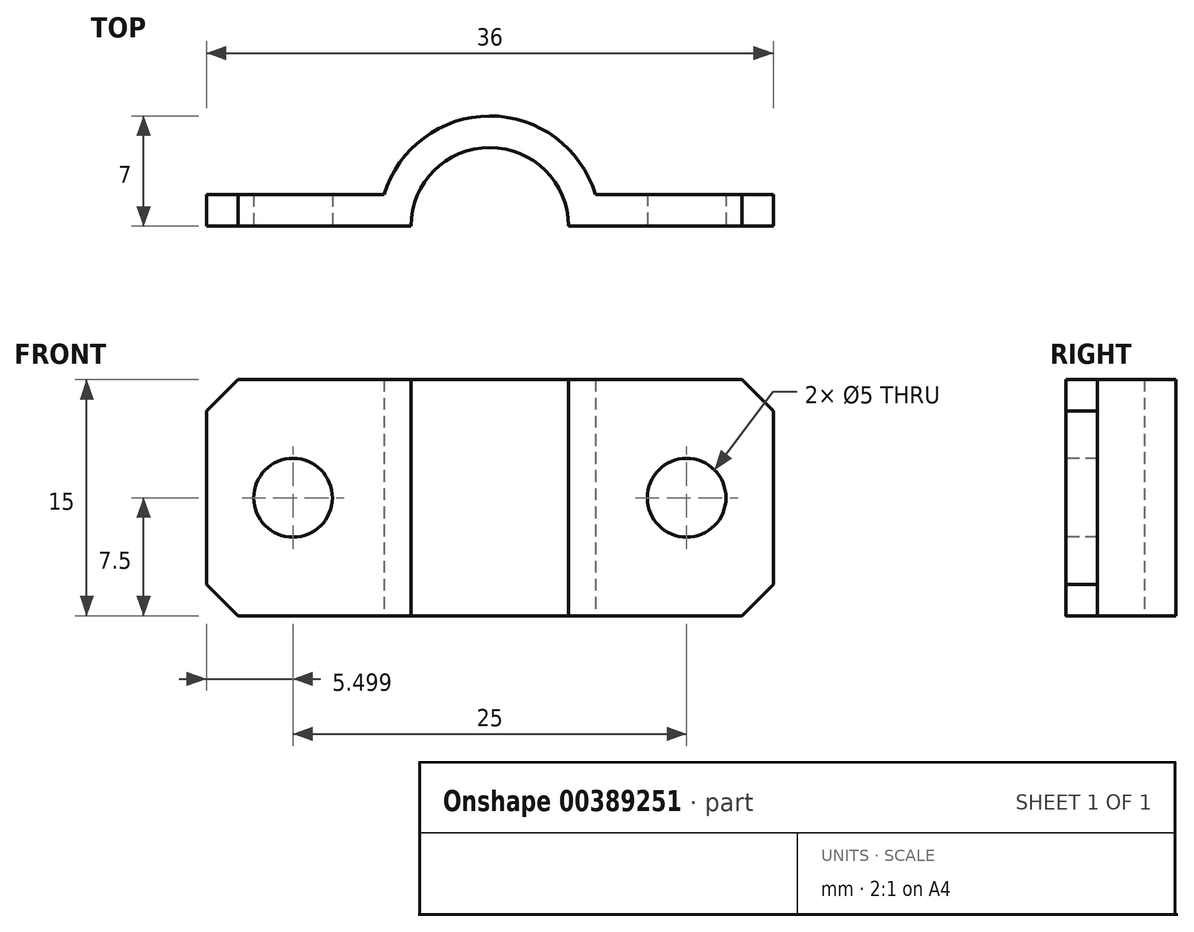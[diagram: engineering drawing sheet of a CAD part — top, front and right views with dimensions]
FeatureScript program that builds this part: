
annotation { "Feature Type Name" : "Feature", "Feature Type Description" : "" }
export const myFeature = defineFeature(function(context is Context, id is Id, definition is map)
    precondition{}
    {
        {
            var Q0;
            Q0=qCreatedBy(makeId("Top.planeOp"),FACE);
            var sketch = newSketch(context, id + "F0", { "sketchPlane" : qUnion([Q0])});
            skLineSegment(sketch, "E0", {"start": v(-47.37, 0) * mm, "end": v(-34.37, 0) * mm});
            skArc(sketch, "E1", {"start": v(-24.37, 0.02) * mm, "mid": v(-29.38, 5) * mm, "end": v(-34.37, 0) * mm});
            skLineSegment(sketch, "E2", {"start": v(-24.37, 0.02) * mm, "end": v(-34.37, 0) * mm, "construction": true});
            skLineSegment(sketch, "E3", {"start": v(-24.37, 0.02) * mm, "end": v(-11.37, 0.02) * mm});
            skLineSegment(sketch, "E4.0", {"start": v(-47.37, 2) * mm, "end": v(-36.08, 2) * mm});
            skArc(sketch, "E4.1", {"start": v(-22.67, 2.02) * mm, "mid": v(-29.38, 7) * mm, "end": v(-36.08, 2) * mm});
            skLineSegment(sketch, "E4.2", {"start": v(-22.67, 2.02) * mm, "end": v(-11.37, 2.02) * mm});
            skLineSegment(sketch, "E5", {"start": v(-11.37, 2.02) * mm, "end": v(-11.37, 0.02) * mm});
            skLineSegment(sketch, "E6", {"start": v(-47.37, 2) * mm, "end": v(-47.37, 0) * mm});
            skSolve(sketch);
        }
        {
            var Q0;
            Q0 = qSketchRegion(id + "F0", true);
            extrude(context, id + "F1", {"entities" : qUnion([Q0]), "depth" : 15 * mm, "offsetDistance" : 25 * mm});
        }
        {
            var Q0;
            Q0=qCreatedBy(makeId("Front.planeOp"),FACE);
            var sketch = newSketch(context, id + "F2", { "sketchPlane" : qUnion([Q0])});
            skLineSegment(sketch, "E7", {"start": v(-41.87, 15) * mm, "end": v(-41.87, 0) * mm, "construction": true});
            skLineSegment(sketch, "E8", {"start": v(-16.87, 15) * mm, "end": v(-16.87, 0) * mm, "construction": true});
            skPoint(sketch, "E9.endSnap0", {"position": v(-41.87, 7.5) * mm});
            skCircle(sketch, "E10", {"center": v(-41.87, 7.5) * mm, "radius": 2.5 * mm});
            skCircle(sketch, "E11", {"center": v(-16.87, 7.5) * mm, "radius": 2.5 * mm});
            skSolve(sketch);
        }
        {
            var Q0;
            Q0 = qSketchRegion(id + "F2", true);
            extrude(context, id + "F3", {"entities" : qUnion([Q0]), "operationType" : NewBodyOperationType.REMOVE, "endBound" : BoundingType.THROUGH_ALL, "oppositeDirection" : true, "depth" : 25 * mm, "offsetDistance" : 25 * mm});
        }
        {
            var Q0;
            Q0=makeQuery(id+"F1.opExtrude","CAP_EDGE",EDGE,{"disambiguationData":[OSD([sQuery(id+"F0.wireOp",EDGE,"E5")])],"isStart":false});
            var Q1;
            Q1=makeQuery(id+"F1.opExtrude","CAP_EDGE",EDGE,{"disambiguationData":[OSD([sQuery(id+"F0.wireOp",EDGE,"E6")])],"isStart":false});
            var Q2;
            Q2=makeQuery(id+"F1.opExtrude","CAP_EDGE",EDGE,{"disambiguationData":[OSD([sQuery(id+"F0.wireOp",EDGE,"E5")])],"isStart":true});
            var Q3;
            Q3=makeQuery(id+"F1.opExtrude","CAP_EDGE",EDGE,{"disambiguationData":[OSD([sQuery(id+"F0.wireOp",EDGE,"E6")])],"isStart":true});
            chamfer(context, id + "F4", {"entities" : qUnion([Q0, Q1, Q2, Q3]), "width" : 2 * mm, "tangentPropagation" : true});
        }
    });
